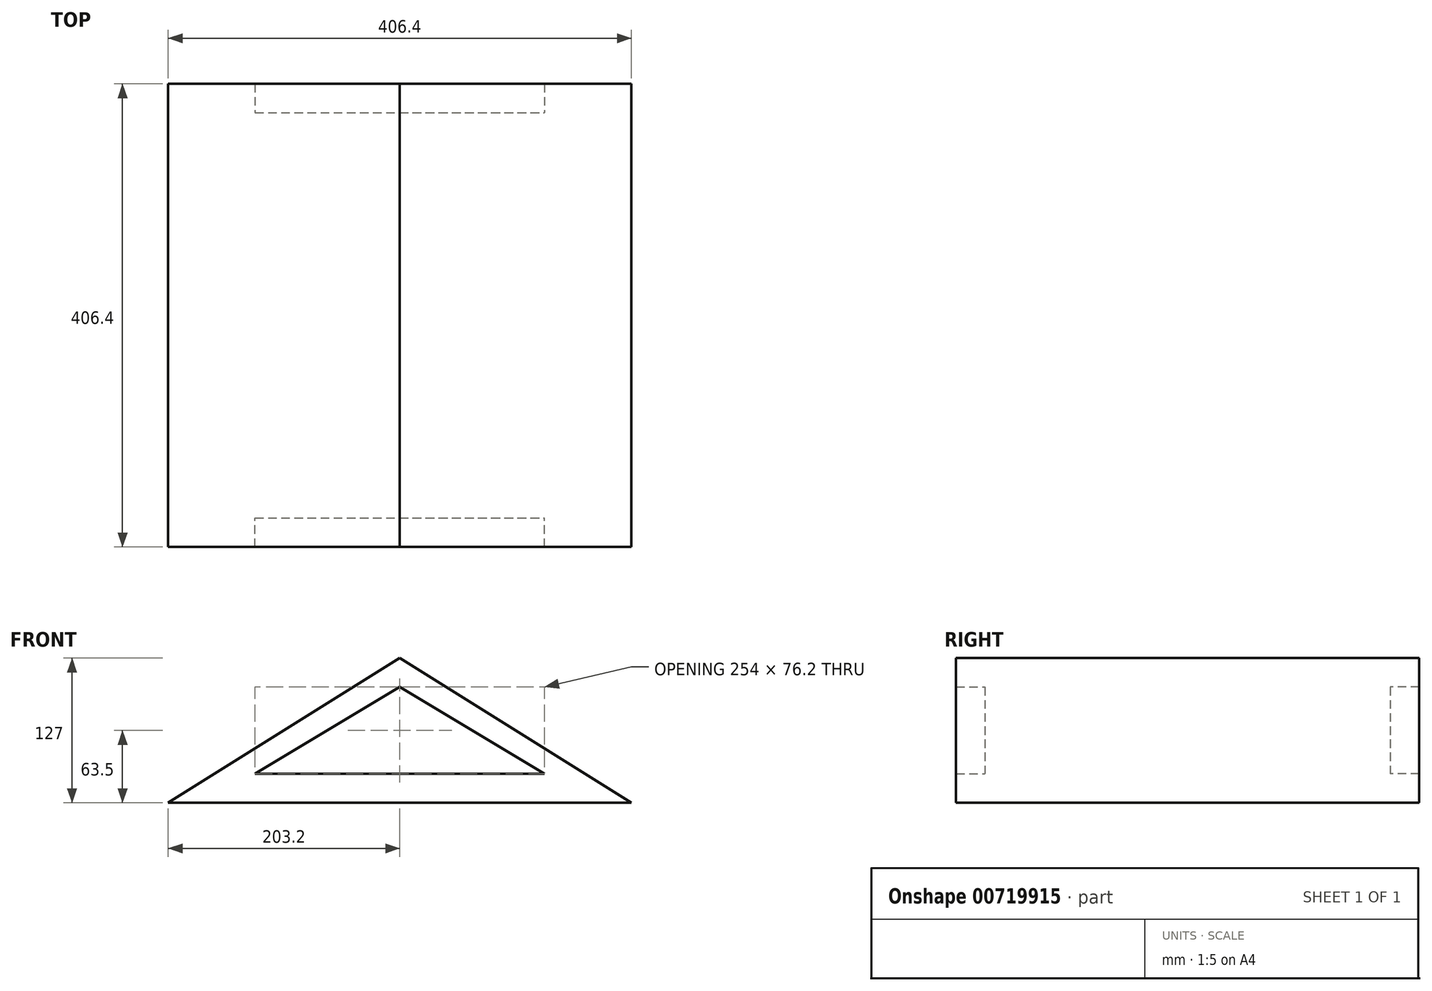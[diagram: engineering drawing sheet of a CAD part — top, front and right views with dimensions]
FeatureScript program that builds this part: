
annotation { "Feature Type Name" : "Feature", "Feature Type Description" : "" }
export const myFeature = defineFeature(function(context is Context, id is Id, definition is map)
    precondition{}
    {
        {
            var Q0;
            Q0=qCreatedBy(makeId("Front.planeOp"),FACE);
            var sketch = newSketch(context, id + "F0", { "sketchPlane" : qUnion([Q0])});
            skLineSegment(sketch, "E0", {"start": v(0, 0) * mm, "end": v(0, 76.2) * mm});
            skLineSegment(sketch, "E1", {"start": v(0, 76.2) * mm, "end": v(0, 0) * mm});
            skLineSegment(sketch, "E2", {"start": v(-203.2, -25.4) * mm, "end": v(203.2, -25.4) * mm});
            skLineSegment(sketch, "E3", {"start": v(0, 101.6) * mm, "end": v(203.2, -25.4) * mm});
            skLineSegment(sketch, "E4", {"start": v(-203.2, -25.4) * mm, "end": v(0, 101.6) * mm});
            skLineSegment(sketch, "E5", {"start": v(-127, 0) * mm, "end": v(127, 0) * mm});
            skLineSegment(sketch, "E6", {"start": v(-127, 0) * mm, "end": v(0, 76.2) * mm});
            skLineSegment(sketch, "E7", {"start": v(0, 76.2) * mm, "end": v(127, 0) * mm});
            skSolve(sketch);
        }
        {
            var Q0;
            {var subQ0=sQuery(id+"F0.wireOp",EDGE,"E0");Q0=makeQuery(id+"F0.imprint","IMPRINT",FACE,{"disambiguationData":[TD([[makeQuery(id+"F0.imprint","IMPRINT",EDGE,{"derivedFrom":subQ0}),1.0]])]});}
            var Q1;
            {var subQ0=sQuery(id+"F0.wireOp",EDGE,"E0");Q1=makeQuery(id+"F0.imprint","IMPRINT",FACE,{"disambiguationData":[TD([[makeQuery(id+"F0.imprint","IMPRINT",EDGE,{"derivedFrom":subQ0}),-1.0]])]});}
            extrude(context, id + "F1", {"entities" : qUnion([Q0, Q1]), "depth" : 177.8 * mm, "offsetDistance" : 25.4 * mm});
        }
        {
            var Q0;
            Q0=makeQuery(id+"F1.opExtrude","CAP_FACE",FACE,{"disambiguationData":[OSD([sQuery(id+"F0.wireOp",EDGE,"E5"),sQuery(id+"F0.wireOp",EDGE,"E6"),sQuery(id+"F0.wireOp",EDGE,"E7")])],"isStart":true});
            extrude(context, id + "F2", {"entities" : qUnion([Q0]), "operationType" : NewBodyOperationType.ADD, "depth" : 177.8 * mm, "offsetDistance" : 25.4 * mm});
        }
        {
            var Q0;
            Q0=makeQuery(id+"F0.imprint","IMPRINT",FACE,{"disambiguationData":[TD([[makeQuery(id+"F0.imprint","IMPRINT",EDGE,{"derivedFrom":sQuery(id+"F0.wireOp",EDGE,"E2")}),1.0]])]});
            extrude(context, id + "F3", {"entities" : qUnion([Q0]), "operationType" : NewBodyOperationType.ADD, "depth" : 203.2 * mm, "offsetDistance" : 25.4 * mm});
        }
        {
            var Q0;
            Q0=makeQuery(id+"F0.imprint","IMPRINT",FACE,{"disambiguationData":[TD([[makeQuery(id+"F0.imprint","IMPRINT",EDGE,{"derivedFrom":sQuery(id+"F0.wireOp",EDGE,"E2")}),1.0]])]});
            extrude(context, id + "F4", {"entities" : qUnion([Q0]), "operationType" : NewBodyOperationType.ADD, "oppositeDirection" : true, "depth" : 203.2 * mm, "offsetDistance" : 25.4 * mm});
        }
    });
